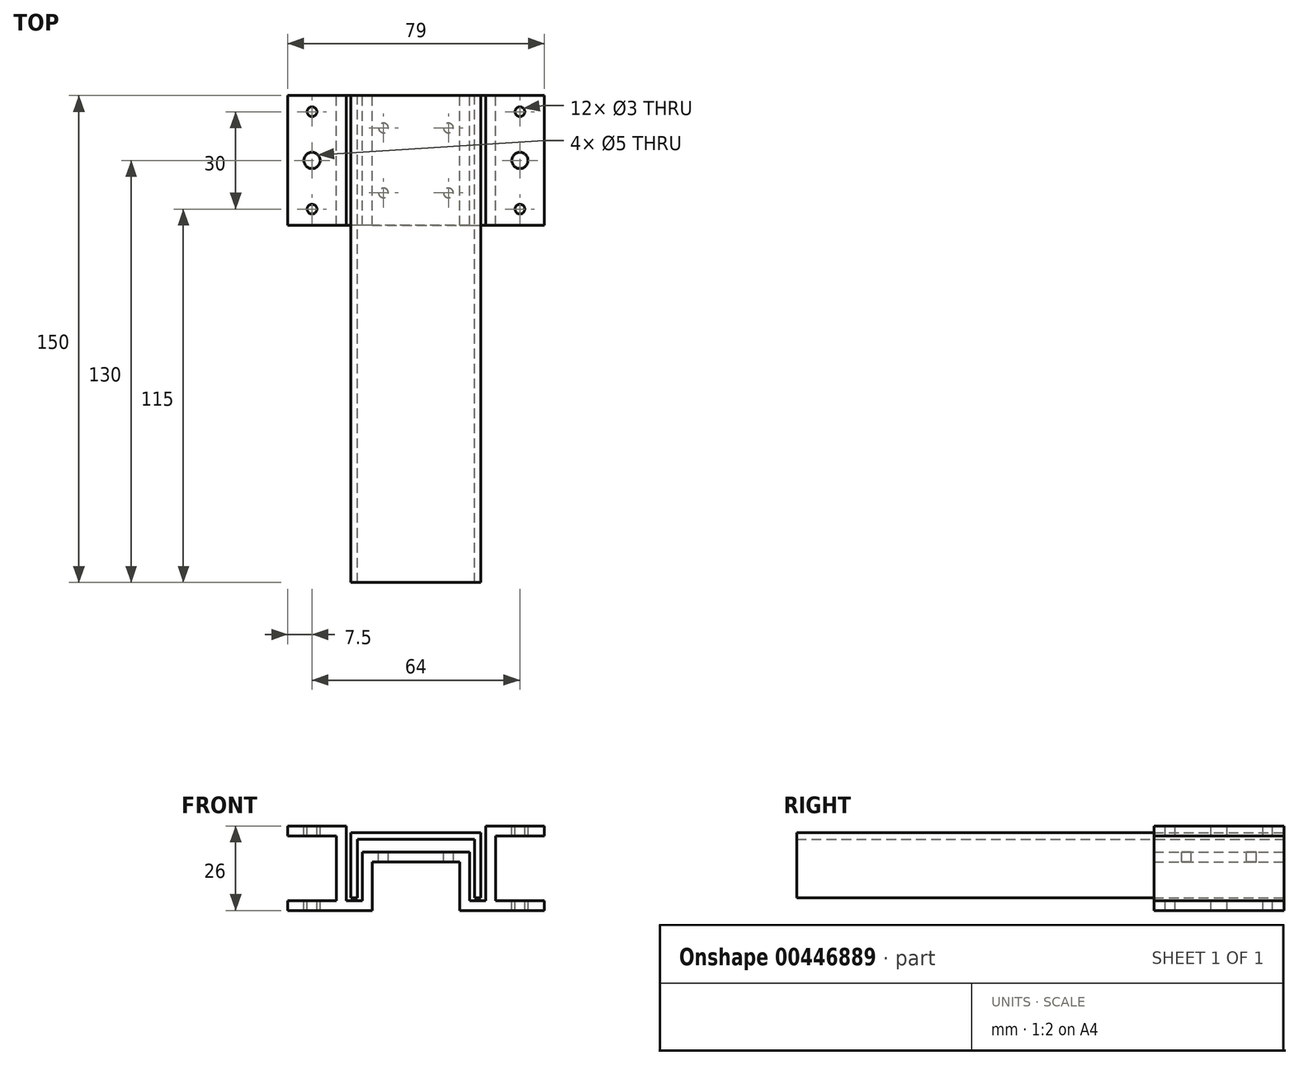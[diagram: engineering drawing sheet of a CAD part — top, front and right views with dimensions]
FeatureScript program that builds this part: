
annotation { "Feature Type Name" : "Feature", "Feature Type Description" : "" }
export const myFeature = defineFeature(function(context is Context, id is Id, definition is map)
    precondition{}
    {
        {
            var Q0;
            Q0=qCreatedBy(makeId("Front.planeOp"),FACE);
            var sketch = newSketch(context, id + "F0", { "sketchPlane" : qUnion([Q0])});
            skLineSegment(sketch, "E0.bottom", {"start": v(13.5, -5) * mm, "end": v(6, -5) * mm, "construction": true});
            skLineSegment(sketch, "E0.top", {"start": v(13.5, 5) * mm, "end": v(-13.5, 5) * mm, "construction": true});
            skLineSegment(sketch, "E0.left", {"start": v(13.5, -5) * mm, "end": v(13.5, 5) * mm, "construction": true});
            skLineSegment(sketch, "E0.right", {"start": v(-13.5, -5) * mm, "end": v(-13.5, 5) * mm, "construction": true});
            skPoint(sketch, "E0.middle", {"position": v(0, 0) * mm});
            skLineSegment(sketch, "E1", {"start": v(-6, -5) * mm, "end": v(-6, 0) * mm, "construction": true});
            skLineSegment(sketch, "E2", {"start": v(-6, 0) * mm, "end": v(6, 0) * mm, "construction": true});
            skLineSegment(sketch, "E3", {"start": v(6, 0) * mm, "end": v(6, -5) * mm, "construction": true});
            skLineSegment(sketch, "E4.trimOffspring", {"start": v(-6, -5) * mm, "end": v(-13.5, -5) * mm, "construction": true});
            skLineSegment(sketch, "E5", {"start": v(-13.5, 6) * mm, "end": v(0, 6) * mm});
            skLineSegment(sketch, "E6", {"start": v(0, 9) * mm, "end": v(-16.5, 9) * mm});
            skLineSegment(sketch, "E7", {"start": v(-16.5, 9) * mm, "end": v(-16.5, -6) * mm});
            skLineSegment(sketch, "E8", {"start": v(-16.5, -6) * mm, "end": v(-21.5, -6) * mm});
            skLineSegment(sketch, "E9", {"start": v(-21.5, -6) * mm, "end": v(-21.5, 17) * mm});
            skLineSegment(sketch, "E10", {"start": v(-21.5, 17) * mm, "end": v(-39.5, 17) * mm});
            skLineSegment(sketch, "E11", {"start": v(-39.5, 17) * mm, "end": v(-39.5, 14) * mm});
            skLineSegment(sketch, "E12", {"start": v(-24.5, -9) * mm, "end": v(-13.5, -9) * mm});
            skLineSegment(sketch, "E13", {"start": v(-13.5, -9) * mm, "end": v(-13.5, 6) * mm});
            skPoint(sketch, "E14", {"position": v(0, 6) * mm});
            skLineSegment(sketch, "E15.bottom", {"start": v(30, 17.34) * mm, "end": v(-30, 17.34) * mm, "construction": true});
            skLineSegment(sketch, "E15.top", {"start": v(30, 27.34) * mm, "end": v(-30, 27.34) * mm, "construction": true});
            skLineSegment(sketch, "E15.left", {"start": v(30, 17.34) * mm, "end": v(30, 27.34) * mm, "construction": true});
            skLineSegment(sketch, "E15.right", {"start": v(-30, 17.34) * mm, "end": v(-30, 27.34) * mm, "construction": true});
            skPoint(sketch, "E16", {"position": v(0, 17.34) * mm});
            skLineSegment(sketch, "E17", {"start": v(0, 6) * mm, "end": v(0, 9) * mm});
            skLineSegment(sketch, "E18", {"start": v(-39.5, 14) * mm, "end": v(-24.5, 14) * mm});
            skLineSegment(sketch, "E19", {"start": v(-24.5, 14) * mm, "end": v(-24.5, -6) * mm});
            skPoint(sketch, "E20.MirrorCS.start.orphan", {"position": v(0, 9) * mm});
            skLineSegment(sketch, "E21", {"start": v(-20, -5.08) * mm, "end": v(-18, -5.08) * mm});
            skLineSegment(sketch, "E22", {"start": v(-18, -5.08) * mm, "end": v(-18, 12.92) * mm});
            skLineSegment(sketch, "E23", {"start": v(-18, 12.92) * mm, "end": v(18, 12.92) * mm});
            skLineSegment(sketch, "E24", {"start": v(18, 12.92) * mm, "end": v(18, -5.08) * mm});
            skLineSegment(sketch, "E25", {"start": v(18, -5.08) * mm, "end": v(20, -5.08) * mm});
            skLineSegment(sketch, "E26", {"start": v(20, -5.08) * mm, "end": v(20, 14.92) * mm});
            skLineSegment(sketch, "E27", {"start": v(20, 14.92) * mm, "end": v(-20, 14.92) * mm});
            skLineSegment(sketch, "E28", {"start": v(-20, 14.92) * mm, "end": v(-20, -5.08) * mm});
            skLineSegment(sketch, "E29", {"start": v(-24.5, -9) * mm, "end": v(-39.5, -9) * mm});
            skLineSegment(sketch, "E30", {"start": v(-39.5, -9) * mm, "end": v(-39.5, -6) * mm});
            skLineSegment(sketch, "E31", {"start": v(-39.5, -6) * mm, "end": v(-24.5, -6) * mm});
            skSolve(sketch);
        }
        {
            var Q0;
            Q0=makeQuery(id+"F0.imprint","IMPRINT",FACE,{"disambiguationData":[TD([[makeQuery(id+"F0.imprint","IMPRINT",EDGE,{"derivedFrom":sQuery(id+"F0.wireOp",EDGE,"E5")}),1.0]])]});
            extrude(context, id + "F1", {"entities" : qUnion([Q0]), "depth" : 40 * mm});
        }
        {
            var Q0;
            Q0=makeQuery(id+"F1.opExtrude","SWEPT_FACE",FACE,{"disambiguationData":[OSD([sQuery(id+"F0.wireOp",EDGE,"E6")])]});
            var sketch = newSketch(context, id + "F2", { "sketchPlane" : qUnion([Q0])});
            skCircle(sketch, "E32", {"center": v(-10, -10) * mm, "radius": 1.5 * mm});
            skCircle(sketch, "E33", {"center": v(-10, -30) * mm, "radius": 1.5 * mm});
            skCircle(sketch, "E34", {"center": v(-10, -10) * mm, "radius": 2.5 * mm});
            skCircle(sketch, "E35", {"center": v(-10, -30) * mm, "radius": 2.5 * mm});
            skSolve(sketch);
        }
        {
            var Q0;
            Q0=makeQuery(id+"F2.imprint","IMPRINT",FACE,{"disambiguationData":[TD([[makeQuery(id+"F2.imprint","IMPRINT",EDGE,{"derivedFrom":sQuery(id+"F2.wireOp",EDGE,"E32")}),1.0]])]});
            var Q1;
            Q1=makeQuery(id+"F2.imprint","IMPRINT",FACE,{"disambiguationData":[TD([[makeQuery(id+"F2.imprint","IMPRINT",EDGE,{"derivedFrom":sQuery(id+"F2.wireOp",EDGE,"E33")}),1.0]])]});
            extrude(context, id + "F3", {"entities" : qUnion([Q0, Q1]), "operationType" : NewBodyOperationType.REMOVE, "endBound" : BoundingType.THROUGH_ALL, "oppositeDirection" : true, "depth" : 25 * mm});
        }
        {
            var Q0;
            Q0=makeQuery(id+"F1.opExtrude","SWEPT_FACE",FACE,{"disambiguationData":[OSD([sQuery(id+"F0.wireOp",EDGE,"E10")])]});
            var sketch = newSketch(context, id + "F4", { "sketchPlane" : qUnion([Q0])});
            skLineSegment(sketch, "E36", {"start": v(-32, 0) * mm, "end": v(-32, -40) * mm, "construction": true});
            skCircle(sketch, "E37", {"center": v(-32, -5) * mm, "radius": 1.5 * mm});
            skCircle(sketch, "E38", {"center": v(-32, -35) * mm, "radius": 1.5 * mm});
            skCircle(sketch, "E39", {"center": v(-32, -20) * mm, "radius": 2.5 * mm});
            skSolve(sketch);
        }
        {
            var Q0;
            Q0=makeQuery(id+"F4.imprint","IMPRINT",FACE,{"disambiguationData":[TD([[makeQuery(id+"F4.imprint","IMPRINT",EDGE,{"derivedFrom":sQuery(id+"F4.wireOp",EDGE,"E38")}),1.0]])]});
            var Q1;
            Q1=makeQuery(id+"F4.imprint","IMPRINT",FACE,{"disambiguationData":[TD([[makeQuery(id+"F4.imprint","IMPRINT",EDGE,{"derivedFrom":sQuery(id+"F4.wireOp",EDGE,"E37")}),1.0]])]});
            var Q2;
            Q2=makeQuery(id+"F4.imprint","IMPRINT",FACE,{"disambiguationData":[TD([[makeQuery(id+"F4.imprint","IMPRINT",EDGE,{"derivedFrom":sQuery(id+"F4.wireOp",EDGE,"E39")}),1.0]])]});
            extrude(context, id + "F5", {"entities" : qUnion([Q0, Q1, Q2]), "operationType" : NewBodyOperationType.REMOVE, "endBound" : BoundingType.THROUGH_ALL, "oppositeDirection" : true, "depth" : 25 * mm});
        }
        {
            var Q0;
            Q0=makeQuery(id+"F1.opExtrude","SWEPT_BODY",BODY,{"disambiguationData":[OSD([sQuery(id+"F0.wireOp",EDGE,"E5"),sQuery(id+"F0.wireOp",EDGE,"E6"),sQuery(id+"F0.wireOp",EDGE,"E7"),sQuery(id+"F0.wireOp",EDGE,"E8"),sQuery(id+"F0.wireOp",EDGE,"E9"),sQuery(id+"F0.wireOp",EDGE,"E10"),sQuery(id+"F0.wireOp",EDGE,"E11"),sQuery(id+"F0.wireOp",EDGE,"E12"),sQuery(id+"F0.wireOp",EDGE,"E13"),sQuery(id+"F0.wireOp",EDGE,"E17"),sQuery(id+"F0.wireOp",EDGE,"E18"),sQuery(id+"F0.wireOp",EDGE,"E19")])]});
            var Q1;
            Q1=makeQuery(id+"F1.opExtrude","SWEPT_FACE",FACE,{"disambiguationData":[OSD([sQuery(id+"F0.wireOp",EDGE,"E17")])]});
            mirror(context, id + "F6", {"operationType" : NewBodyOperationType.ADD, "entities" : qUnion([Q0]), "mirrorPlane" : qUnion([Q1])});
        }
        {
            var Q0;
            Q0=makeQuery(id+"F0.imprint","IMPRINT",FACE,{"disambiguationData":[TD([[makeQuery(id+"F0.imprint","IMPRINT",EDGE,{"derivedFrom":sQuery(id+"F0.wireOp",EDGE,"E21")}),1.0]])]});
            extrude(context, id + "F7", {"entities" : qUnion([Q0]), "depth" : 150 * mm});
        }
    });
